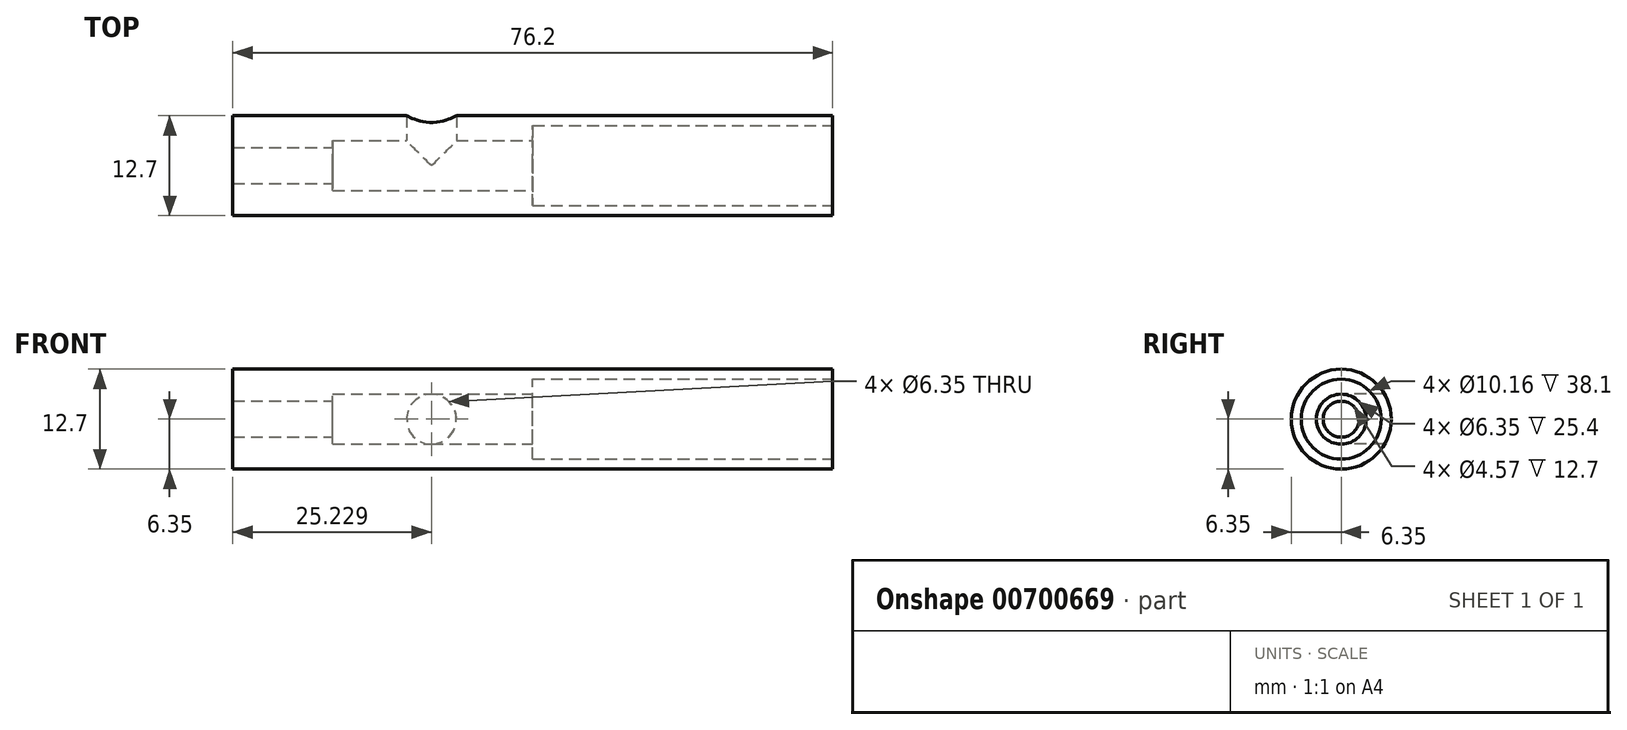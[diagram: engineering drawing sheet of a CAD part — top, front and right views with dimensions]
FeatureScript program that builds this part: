
annotation { "Feature Type Name" : "Feature", "Feature Type Description" : "" }
export const myFeature = defineFeature(function(context is Context, id is Id, definition is map)
    precondition{}
    {
        {
            var Q0;
            Q0=qCreatedBy(makeId("Right.planeOp"),FACE);
            var sketch = newSketch(context, id + "F0", { "sketchPlane" : qUnion([Q0])});
            skCircle(sketch, "E0", {"center": v(0, 0) * mm, "radius": 6.35 * mm});
            skSolve(sketch);
        }
        {
            var Q0;
            Q0 = qSketchRegion(id + "F0", true);
            extrude(context, id + "F1", {"entities" : qUnion([Q0]), "depth" : 76.2 * mm, "offsetDistance" : 25.4 * mm});
        }
        {
            var Q0;
            Q0=makeQuery(id+"F1.opExtrude","CAP_FACE",FACE,{"disambiguationData":[OSD([sQuery(id+"F0.wireOp",EDGE,"E0")])],"isStart":false});
            var sketch = newSketch(context, id + "F2", { "sketchPlane" : qUnion([Q0])});
            skCircle(sketch, "E1", {"center": v(0, 0) * mm, "radius": 5.08 * mm});
            skSolve(sketch);
        }
        {
            var Q0;
            Q0 = qSketchRegion(id + "F2", true);
            extrude(context, id + "F3", {"entities" : qUnion([Q0]), "operationType" : NewBodyOperationType.REMOVE, "oppositeDirection" : true, "depth" : 38.1 * mm, "offsetDistance" : 25.4 * mm});
        }
        {
            var Q0;
            Q0=makeQuery(id+"F3.boolean.opBoolean","COPY",FACE,{"derivedFrom":makeQuery(id+"F3.opExtrude","CAP_FACE",FACE,{"disambiguationData":[OSD([sQuery(id+"F2.wireOp",EDGE,"E1")])],"isStart":false})});
            var sketch = newSketch(context, id + "F4", { "sketchPlane" : qUnion([Q0])});
            skCircle(sketch, "E2", {"center": v(0, 0) * mm, "radius": 3.18 * mm});
            skSolve(sketch);
        }
        {
            var Q0;
            Q0 = qSketchRegion(id + "F4", true);
            extrude(context, id + "F5", {"entities" : qUnion([Q0]), "operationType" : NewBodyOperationType.REMOVE, "oppositeDirection" : true, "depth" : 25.4 * mm, "offsetDistance" : 25.4 * mm});
        }
        {
            var Q0;
            Q0=makeQuery(id+"F5.boolean.opBoolean","COPY",FACE,{"derivedFrom":makeQuery(id+"F5.opExtrude","CAP_FACE",FACE,{"disambiguationData":[OSD([sQuery(id+"F4.wireOp",EDGE,"E2")])],"isStart":false})});
            var sketch = newSketch(context, id + "F6", { "sketchPlane" : qUnion([Q0])});
            skCircle(sketch, "E3", {"center": v(0, 0) * mm, "radius": 2.29 * mm});
            skSolve(sketch);
        }
        {
            var Q0;
            Q0 = qSketchRegion(id + "F6", true);
            extrude(context, id + "F7", {"entities" : qUnion([Q0]), "operationType" : NewBodyOperationType.REMOVE, "oppositeDirection" : true, "depth" : 25.4 * mm, "offsetDistance" : 25.4 * mm});
        }
        {
            var Q0;
            Q0=qCreatedBy(makeId("Front.planeOp"),FACE);
            var sketch = newSketch(context, id + "F8", { "sketchPlane" : qUnion([Q0])});
            skPoint(sketch, "E4", {"position": v(25.23, 0) * mm});
            skCircle(sketch, "E5", {"center": v(25.23, 0) * mm, "radius": 3.18 * mm});
            skSolve(sketch);
        }
        {
            var Q0;
            Q0 = qSketchRegion(id + "F8", true);
            extrude(context, id + "F9", {"entities" : qUnion([Q0]), "operationType" : NewBodyOperationType.REMOVE, "oppositeDirection" : true, "depth" : 25.4 * mm, "offsetDistance" : 25.4 * mm});
        }
    });
